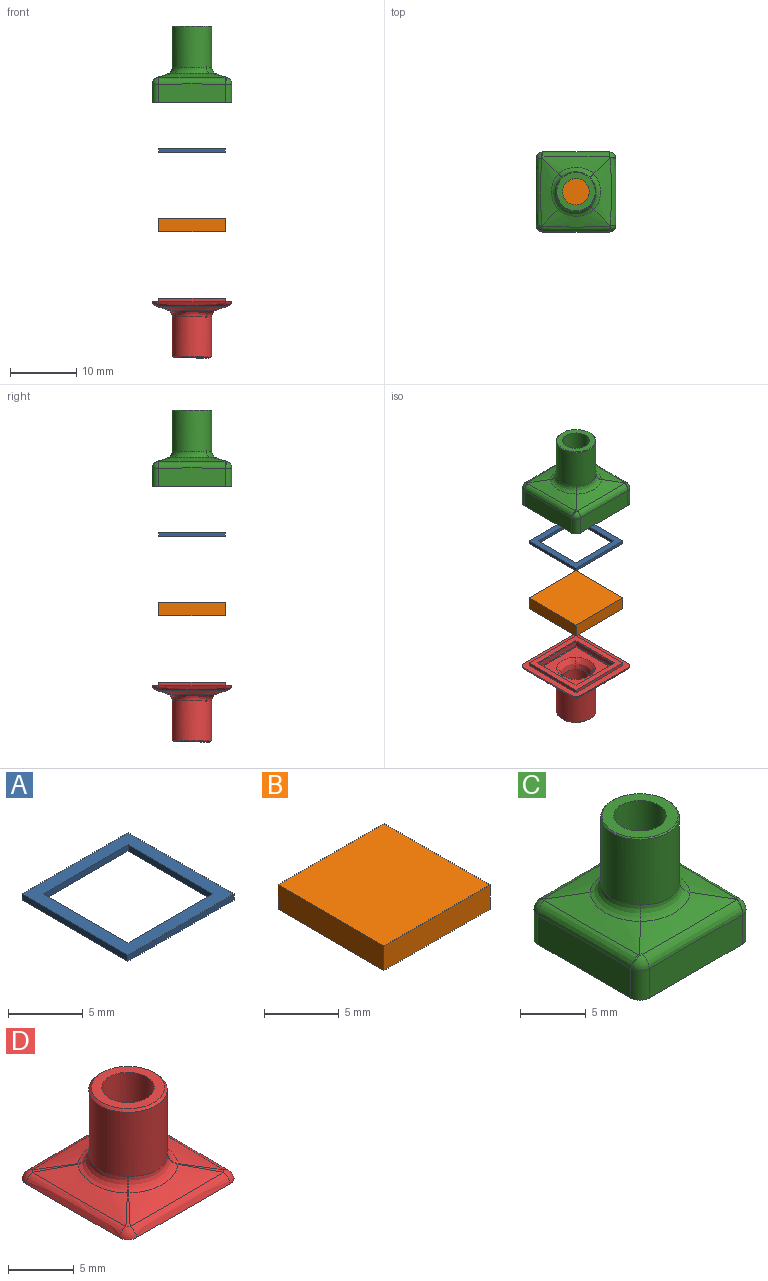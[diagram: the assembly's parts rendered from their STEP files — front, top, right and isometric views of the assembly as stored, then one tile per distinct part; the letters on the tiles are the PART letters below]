
ASSEMBLY  parts=4 mates=4
PART A: 10 faces, bbox 10x10x0.5 mm
  f0: plane 10x0.5mm, normal (0,-1,0), area 5mm2, adj f1,f7,f8,f9
  f1: plane 10x0.5mm, normal (1,0,0), area 5mm2, adj f0,f2,f8,f9
  f2: plane 10x0.5mm, normal (0,1,0), area 5mm2, adj f1,f7,f8,f9
  f3: plane 8x0.5mm, normal (0,1,0), area 4mm2, adj f4,f6,f8,f9
  f4: plane 8x0.5mm, normal (1,0,0), area 4mm2, adj f3,f5,f8,f9
  f5: plane 8x0.5mm, normal (0,-1,0), area 4mm2, adj f4,f6,f8,f9
  f6: plane 8x0.5mm, normal (-1,0,0), area 4mm2, adj f3,f5,f8,f9
  f7: plane 10x0.5mm, normal (-1,0,0), area 5mm2, adj f0,f2,f8,f9
  f8: plane 10x10mm, normal (0,0,1), area 36mm2, adj f0,f1,f2,f3,f4,f5,f6,f7
  f9: plane 10x10mm, normal (0,0,-1), area 36mm2, adj f0,f1,f2,f3,f4,f5,f6,f7
PART B: 6 faces, bbox 10x10x2 mm
  f0: plane 10x2mm, normal (0,-1,0), area 20mm2, adj f1,f3,f4,f5
  f1: plane 10x2mm, normal (1,0,0), area 20mm2, adj f0,f2,f4,f5
  f2: plane 10x2mm, normal (0,1,0), area 20mm2, adj f1,f3,f4,f5
  f3: plane 10x2mm, normal (-1,0,0), area 20mm2, adj f0,f2,f4,f5
  f4: plane 10x10mm, normal (0,0,1), area 100mm2, adj f0,f1,f2,f3
  f5: plane 10x10mm, normal (0,0,-1), area 100mm2, adj f0,f1,f2,f3
PART C: 51 faces, bbox 13.1x13.1x11.5 mm
  f0: cylinder r=3mm len=6.07mm, axis (0,0,-1), area 114.3mm2, adj f34,f35,f36,f37,f38
  f1: plane 5.8x5.8mm, normal (0,0,1), area 13.9mm2, adj f11,f38
  f2: plane 9.8x9.8mm, normal (0,0,-1), area 32mm2, adj f39,f40,f41,f42,f47,f48,f49,f50
  f3: plane 10x2.78mm, normal (1,0,0), area 27.6mm2, adj f14,f18,f21,f24
  f4: plane 10x2.78mm, normal (0,1,0), area 27.6mm2, adj f14,f18,f19,f25
  f5: plane 10x2.78mm, normal (-1,0,0), area 27.6mm2, adj f14,f19,f20,f31
  f6: plane 10x2.78mm, normal (0,-1,0), area 27.6mm2, adj f14,f20,f21,f30
  f7: bspline ~12.45x3.94mm, area 18.2mm2, adj f8,f10,f22,f24,f28,f34
  f8: bspline ~12.45x3.94mm, area 18.2mm2, adj f7,f9,f28,f30,f33,f35
  f9: bspline ~12.45x3.94mm, area 18.2mm2, adj f8,f10,f27,f31,f33,f37
  f10: bspline ~12.45x3.94mm, area 18.2mm2, adj f7,f9,f22,f25,f27,f36
  f11: cylinder r=2mm len=6.32mm, axis (0,0,-1), area 79.5mm2, adj f1,f43,f44,f45,f46
  f12: plane 5.83x5.83mm, normal (0,0,-1), area 7.8mm2, adj f39,f40,f41,f42,f43,f44,f45,f46
  f13: plane 10x2.9mm, normal (0,1,0), area 29mm2, adj f14,f15,f16,f48
  f14: plane 12x12mm, normal (0,0,-1), area 43.1mm2, adj f3,f4,f5,f6,f13,f15,f16,f17
  f15: plane 10x2.9mm, normal (1,0,0), area 29mm2, adj f13,f14,f17,f50
  f16: plane 10x2.9mm, normal (-1,0,0), area 29mm2, adj f13,f14,f17,f47
  f17: plane 10x2.9mm, normal (0,-1,0), area 29mm2, adj f14,f15,f16,f49
  f18: cylinder r=1mm len=2.73mm, axis (0,0,-1), area 4.3mm2, adj f3,f4,f14,f23
  f19: cylinder r=1mm len=2.73mm, axis (0,0,1), area 4.3mm2, adj f4,f5,f14,f29
  f20: cylinder r=1mm len=2.73mm, axis (0,0,-1), area 4.3mm2, adj f5,f6,f14,f32
  f21: cylinder r=1mm len=2.73mm, axis (0,0,1), area 4.3mm2, adj f3,f6,f14,f26
  f22: bspline ~2.68x1.55mm, area 0.1mm2, adj f7,f10,f23,f24
  f23: sphere r=1mm, area 1.4mm2, adj f18,f22,f25
  f24: bspline ~13.06x1.02mm, area 12.9mm2, adj f3,f7,f22,f26
  f25: bspline ~13.06x1.02mm, area 12.9mm2, adj f4,f10,f23,f27
  f26: sphere r=1mm, area 1.3mm2, adj f21,f24,f28
  f27: bspline ~2.68x1.55mm, area 0.1mm2, adj f9,f10,f25,f29
  f28: bspline ~2.68x1.55mm, area 0.1mm2, adj f7,f8,f26,f30
  f29: sphere r=1mm, area 1.4mm2, adj f19,f27,f31
  f30: bspline ~13.06x1.02mm, area 12.9mm2, adj f6,f8,f28,f32
  f31: bspline ~13.06x1.02mm, area 12.9mm2, adj f5,f9,f29,f33
  f32: sphere r=1mm, area 1.3mm2, adj f20,f30,f33
  f33: bspline ~2.68x1.55mm, area 0.1mm2, adj f8,f9,f31,f32
  f34: bspline ~5.89x1.78mm, area 6.7mm2, adj f0,f7,f35,f36
  f35: bspline ~5.89x1.78mm, area 6.7mm2, adj f0,f8,f34,f37
  f36: bspline ~5.89x1.78mm, area 6.7mm2, adj f0,f10,f34,f37
  f37: bspline ~5.89x1.78mm, area 6.7mm2, adj f0,f9,f35,f36
  f38: cone r=2.9mm half-angle=45deg, axis (0,0,-1), area 2.6mm2, adj f0,f1
  f39: plane 8x1.1mm, normal (0.41,0,-0.91), area 8.3mm2, adj f2,f12,f40,f41
  f40: plane 8x1.1mm, normal (0,-0.41,-0.91), area 8.3mm2, adj f2,f12,f39,f42
  f41: plane 8x1.1mm, normal (0,0.41,-0.91), area 8.3mm2, adj f2,f12,f39,f42
  f42: plane 8x1.1mm, normal (-0.41,0,-0.91), area 8.3mm2, adj f2,f12,f40,f41
  f43: bspline ~4.69x1.7mm, area 7mm2, adj f11,f12,f44,f45
  f44: bspline ~4.69x1.7mm, area 7mm2, adj f11,f12,f43,f46
  f45: bspline ~4.69x1.7mm, area 7mm2, adj f11,f12,f43,f46
  f46: bspline ~4.69x1.7mm, area 7mm2, adj f11,f12,f44,f45
  f47: plane 10x0.1mm, normal (-0.71,0,-0.71), area 1.4mm2, adj f2,f16,f48,f49
  f48: plane 10x0.1mm, normal (0,0.71,-0.71), area 1.4mm2, adj f2,f13,f47,f50
  f49: plane 10x0.1mm, normal (0,-0.71,-0.71), area 1.4mm2, adj f2,f17,f47,f50
  f50: plane 10x0.1mm, normal (0.71,0,-0.71), area 1.4mm2, adj f2,f15,f48,f49
PART D: 51 faces, bbox 13.4x13.4x9 mm
  f0: plane 10x10mm, normal (0,0,-1), area 32.8mm2, adj f3,f4,f5,f6,f39,f40,f41,f42
  f1: cylinder r=3mm len=6.08mm, axis (0,0,-1), area 113.7mm2, adj f18,f31,f32,f33,f34,f35,f36,f37
  f2: plane 5.6x5.6mm, normal (0,0,1), area 12.1mm2, adj f12,f18
  f3: plane 10x0.5mm, normal (0,1,0), area 5mm2, adj f0,f4,f6,f7
  f4: plane 10x0.5mm, normal (-1,0,0), area 5mm2, adj f0,f3,f5,f7
  f5: plane 10x0.5mm, normal (0,-1,0), area 5mm2, adj f0,f4,f6,f7
  f6: plane 10x0.5mm, normal (1,0,0), area 5mm2, adj f0,f3,f5,f7
  f7: plane 12x12mm, normal (0,0,-1), area 43.2mm2, adj f3,f4,f5,f6,f19,f20,f21,f22
  f8: bspline ~12x3.88mm, area 18.9mm2, adj f20,f24,f28,f36
  f9: bspline ~12x3.88mm, area 18.9mm2, adj f22,f28,f30,f32
  f10: bspline ~12x3.88mm, area 18.9mm2, adj f21,f26,f30,f33
  f11: bspline ~12x3.88mm, area 18.9mm2, adj f19,f24,f26,f37
  f12: cylinder r=2mm len=6.32mm, axis (0,0,-1), area 79.5mm2, adj f2,f43,f44,f45,f46
  f13: plane 7.83x7.83mm, normal (0,0,-1), area 35mm2, adj f43,f44,f45,f46,f47,f48,f49,f50
  f14: plane 8x0.8mm, normal (-1,0,0), area 6.4mm2, adj f15,f17,f40,f47
  f15: plane 8x0.8mm, normal (0,-1,0), area 6.4mm2, adj f14,f16,f42,f48
  f16: plane 8x0.8mm, normal (1,0,0), area 6.4mm2, adj f15,f17,f41,f50
  f17: plane 8x0.8mm, normal (0,1,0), area 6.4mm2, adj f14,f16,f39,f49
  f18: cone r=2.8mm half-angle=45deg, axis (0,0,-1), area 5.2mm2, adj f1,f2
  f19: bspline ~13.33x0.75mm, area 10.4mm2, adj f7,f11,f23,f25
  f20: bspline ~13.33x0.75mm, area 10.4mm2, adj f7,f8,f23,f27
  f21: bspline ~13.33x0.75mm, area 10.4mm2, adj f7,f10,f25,f29
  f22: bspline ~13.33x0.75mm, area 10.4mm2, adj f7,f9,f27,f29
  f23: sphere r=1mm, area 1mm2, adj f7,f19,f20,f24
  f24: bspline ~3.54x3.54mm, area 0.8mm2, adj f8,f11,f23,f38
  f25: sphere r=1mm, area 1mm2, adj f7,f19,f21,f26
  f26: bspline ~3.54x3.54mm, area 0.8mm2, adj f10,f11,f25,f35
  f27: sphere r=1mm, area 1mm2, adj f7,f20,f22,f28
  f28: bspline ~3.54x3.54mm, area 0.8mm2, adj f8,f9,f27,f34
  f29: sphere r=1mm, area 1mm2, adj f7,f21,f22,f30
  f30: bspline ~3.54x3.54mm, area 0.8mm2, adj f9,f10,f29,f31
  f31: bspline ~1.01x0.95mm, area 0.1mm2, adj f1,f30,f32,f33
  f32: bspline ~6.52x2.07mm, area 6.5mm2, adj f1,f9,f31,f34
  f33: bspline ~6.52x2.07mm, area 6.5mm2, adj f1,f10,f31,f35
  f34: bspline ~1.01x0.95mm, area 0.1mm2, adj f1,f28,f32,f36
  f35: bspline ~1.01x0.95mm, area 0.1mm2, adj f1,f26,f33,f37
  f36: bspline ~6.52x2.07mm, area 6.5mm2, adj f1,f8,f34,f38
  f37: bspline ~6.52x2.07mm, area 6.5mm2, adj f1,f11,f35,f38
  f38: bspline ~1x0.84mm, area 0.1mm2, adj f1,f24,f36,f37
  f39: plane 8.2x0.1mm, normal (0,0.71,-0.71), area 1.1mm2, adj f0,f17,f40,f41
  f40: plane 8.2x0.1mm, normal (-0.71,0,-0.71), area 1.1mm2, adj f0,f14,f39,f42
  f41: plane 8.2x0.1mm, normal (0.71,0,-0.71), area 1.1mm2, adj f0,f16,f39,f42
  f42: plane 8.2x0.1mm, normal (0,-0.71,-0.71), area 1.1mm2, adj f0,f15,f40,f41
  f43: bspline ~4.69x1.7mm, area 7mm2, adj f12,f13,f44,f45
  f44: bspline ~4.69x1.7mm, area 7mm2, adj f12,f13,f43,f46
  f45: bspline ~4.69x1.7mm, area 7mm2, adj f12,f13,f43,f46
  f46: bspline ~4.69x1.7mm, area 7mm2, adj f12,f13,f44,f45
  f47: plane 8x0.1mm, normal (-0.71,0,-0.71), area 1.1mm2, adj f13,f14,f48,f49
  f48: plane 8x0.1mm, normal (0,-0.71,-0.71), area 1.1mm2, adj f13,f15,f47,f50
  f49: plane 8x0.1mm, normal (0,0.71,-0.71), area 1.1mm2, adj f13,f17,f47,f50
  f50: plane 8x0.1mm, normal (0.71,0,-0.71), area 1.1mm2, adj f13,f16,f48,f49
PLACE A t=(22.02,-20.31,17.39)mm
PLACE B t=(22.02,-20.31,6.39)mm
PLACE C t=(22.02,-20.31,26.39)mm
PLACE D rot(axis=(-0.71,-0.71,0),180deg) t=(22.02,-20.31,-3.61)mm
MATE parallel A.f9 <-> B.f4  axis (0,0,-1) through (27.02,-15.31,17.39)mm
MATE parallel C.f19 <-> D.f7  axis (0,0,-1) through (17.02,-15.31,24.89)mm
MATE parallel B.f5 <-> D.f0  axis (0,0,-1) through (27.02,-15.31,5.39)mm
MATE parallel A.f9 <-> B.f4  axis (0,0,-1) through (27.02,-15.31,17.39)mm
